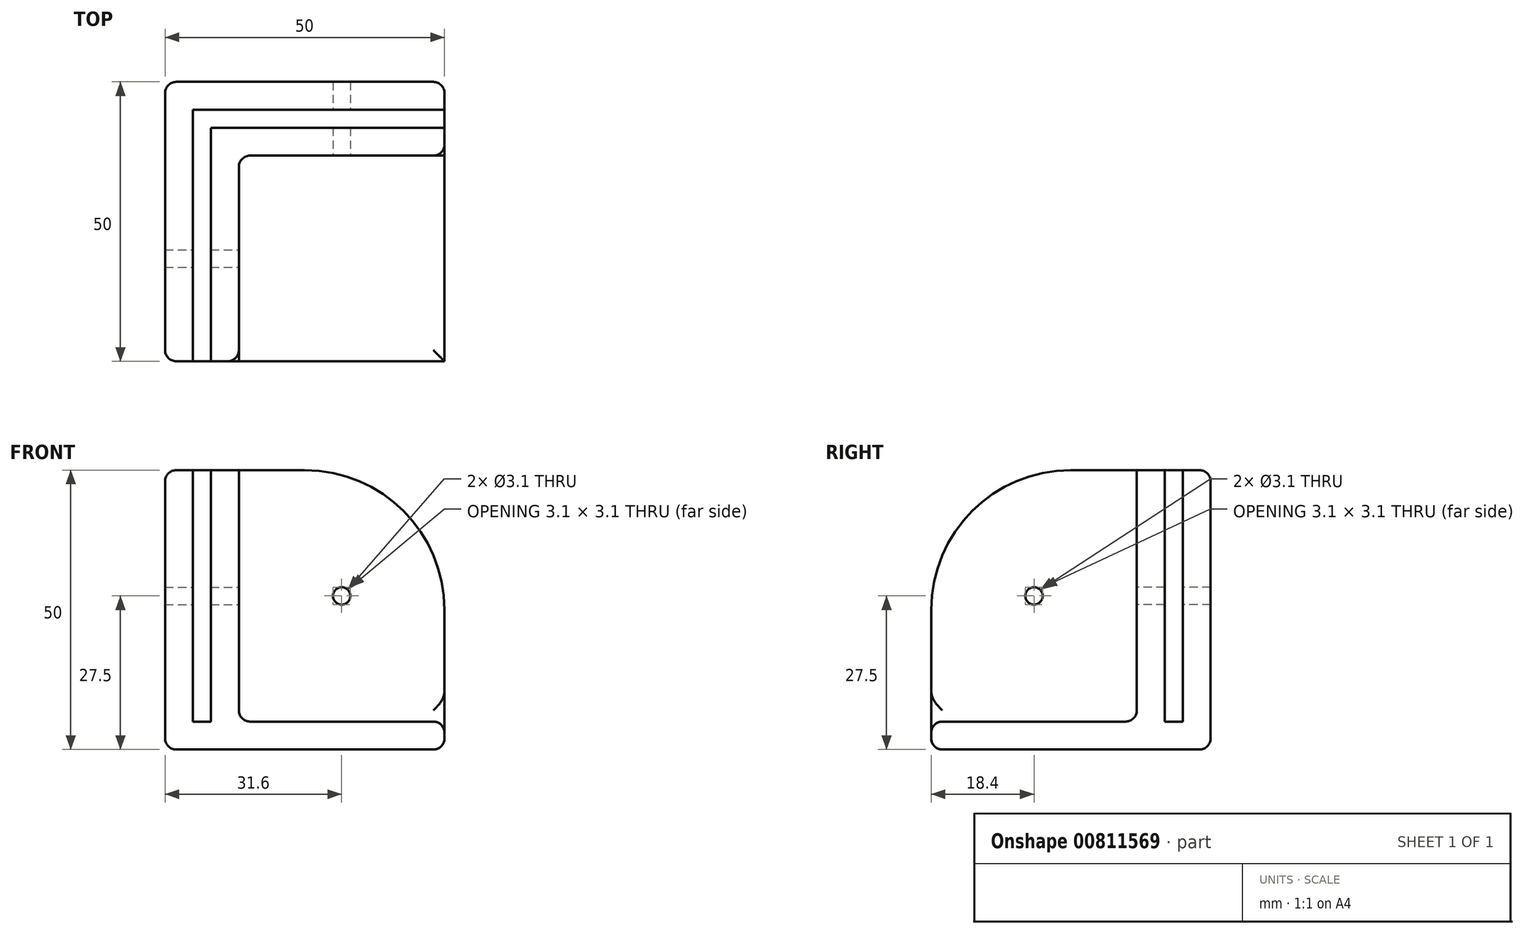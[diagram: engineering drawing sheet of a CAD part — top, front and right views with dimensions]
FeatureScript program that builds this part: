
annotation { "Feature Type Name" : "Feature", "Feature Type Description" : "" }
export const myFeature = defineFeature(function(context is Context, id is Id, definition is map)
    precondition{}
    {
        {
            var Q0;
            Q0=qCreatedBy(makeId("Top.planeOp"),FACE);
            var sketch = newSketch(context, id + "F0", { "sketchPlane" : qUnion([Q0])});
            skLineSegment(sketch, "E0.bottom", {"start": v(25, -25) * mm, "end": v(-25, -25) * mm});
            skLineSegment(sketch, "E0.top", {"start": v(25, 25) * mm, "end": v(-25, 25) * mm});
            skLineSegment(sketch, "E0.left", {"start": v(25, -25) * mm, "end": v(25, 25) * mm});
            skLineSegment(sketch, "E0.right", {"start": v(-25, -25) * mm, "end": v(-25, 25) * mm});
            skPoint(sketch, "E0.middle", {"position": v(0, 0) * mm});
            skSolve(sketch);
        }
        {
            var Q0;
            Q0=qSketchRegion(id+"F0",true);
            extrude(context, id + "F1", {"entities" : qUnion([Q0]), "depth" : 5 * mm, "offsetDistance" : 25 * mm});
        }
        {
            var Q0;
            Q0=makeQuery(id+"F1.opExtrude","CAP_FACE",FACE,{"disambiguationData":[OSD([sQuery(id+"F0.wireOp",EDGE,"E0.bottom"),sQuery(id+"F0.wireOp",EDGE,"E0.top"),sQuery(id+"F0.wireOp",EDGE,"E0.left"),sQuery(id+"F0.wireOp",EDGE,"E0.right")])],"isStart":false});
            var sketch = newSketch(context, id + "F2", { "sketchPlane" : qUnion([Q0])});
            skLineSegment(sketch, "E1.bottom", {"start": v(-25, 25) * mm, "end": v(-20, 25) * mm});
            skLineSegment(sketch, "E1.top", {"start": v(-25, -25) * mm, "end": v(-20, -25) * mm});
            skLineSegment(sketch, "E1.left", {"start": v(-25, 25) * mm, "end": v(-25, -25) * mm});
            skLineSegment(sketch, "E1.right", {"start": v(-20, 25) * mm, "end": v(-20, -25) * mm});
            skLineSegment(sketch, "E2.bottom", {"start": v(-20, 25) * mm, "end": v(25, 25) * mm});
            skLineSegment(sketch, "E2.top", {"start": v(-20, 20) * mm, "end": v(25, 20) * mm});
            skLineSegment(sketch, "E2.left", {"start": v(-20, 25) * mm, "end": v(-20, 20) * mm});
            skLineSegment(sketch, "E2.right", {"start": v(25, 25) * mm, "end": v(25, 20) * mm});
            skSolve(sketch);
        }
        {
            var Q0;
            Q0=qSketchRegion(id+"F2",true);
            extrude(context, id + "F3", {"entities" : qUnion([Q0]), "operationType" : NewBodyOperationType.ADD, "depth" : 45 * mm, "offsetDistance" : 25 * mm});
        }
        {
            var Q0;
            Q0=makeQuery(id+"F1.opExtrude","CAP_FACE",FACE,{"disambiguationData":[OSD([sQuery(id+"F0.wireOp",EDGE,"E0.bottom"),sQuery(id+"F0.wireOp",EDGE,"E0.top"),sQuery(id+"F0.wireOp",EDGE,"E0.left"),sQuery(id+"F0.wireOp",EDGE,"E0.right")])],"isStart":false});
            var sketch = newSketch(context, id + "F4", { "sketchPlane" : qUnion([Q0])});
            skLineSegment(sketch, "E3.bottom", {"start": v(-16.8, -25) * mm, "end": v(-11.8, -25) * mm});
            skLineSegment(sketch, "E3.top", {"start": v(-16.8, 16.8) * mm, "end": v(-11.8, 16.8) * mm});
            skLineSegment(sketch, "E3.left", {"start": v(-16.8, -25) * mm, "end": v(-16.8, 16.8) * mm});
            skLineSegment(sketch, "E3.right", {"start": v(-11.8, -25) * mm, "end": v(-11.8, 16.8) * mm});
            skLineSegment(sketch, "E4.bottom", {"start": v(-11.8, 16.8) * mm, "end": v(25, 16.8) * mm});
            skLineSegment(sketch, "E4.top", {"start": v(-11.8, 11.8) * mm, "end": v(25, 11.8) * mm});
            skLineSegment(sketch, "E4.left", {"start": v(-11.8, 16.8) * mm, "end": v(-11.8, 11.8) * mm});
            skLineSegment(sketch, "E4.right", {"start": v(25, 16.8) * mm, "end": v(25, 11.8) * mm});
            skSolve(sketch);
        }
        {
            var Q0;
            Q0=qSketchRegion(id+"F4",true);
            var Q1;
            Q1=makeQuery(id+"F3.opExtrude","CAP_FACE",FACE,{"disambiguationData":[OSD([sQuery(id+"F2.wireOp",EDGE,"E1.bottom"),sQuery(id+"F2.wireOp",EDGE,"E1.top"),sQuery(id+"F2.wireOp",EDGE,"E1.left"),sQuery(id+"F2.wireOp",EDGE,"E1.right"),sQuery(id+"F2.wireOp",EDGE,"E2.bottom"),sQuery(id+"F2.wireOp",EDGE,"E2.top"),sQuery(id+"F2.wireOp",EDGE,"E2.right")])],"isStart":false});
            extrude(context, id + "F5", {"entities" : qUnion([Q0]), "operationType" : NewBodyOperationType.ADD, "endBound" : BoundingType.UP_TO_SURFACE, "depth" : 25 * mm, "endBoundEntityFace" : qUnion([Q1]), "offsetDistance" : 25 * mm});
        }
        {
            var Q0;
            Q0=makeQuery(id+"F3.opExtrude","CAP_EDGE",EDGE,{"disambiguationData":[OSD([sQuery(id+"F2.wireOp",EDGE,"E1.top")])],"isStart":false});
            var Q1;
            Q1=makeQuery(id+"F5.opExtrude","CAP_EDGE",EDGE,{"disambiguationData":[OSD([sQuery(id+"F4.wireOp",EDGE,"E3.bottom")])],"isStart":false});
            var Q2;
            Q2=makeQuery(id+"F5.opExtrude","CAP_EDGE",EDGE,{"disambiguationData":[OSD([sQuery(id+"F4.wireOp",EDGE,"E4.right")])],"isStart":false});
            var Q3;
            Q3=makeQuery(id+"F3.opExtrude","CAP_EDGE",EDGE,{"disambiguationData":[OSD([sQuery(id+"F2.wireOp",EDGE,"E2.right")])],"isStart":false});
            fillet(context, id + "F6", {"entities" : qUnion([Q0, Q1, Q2, Q3]), "radius" : 25 * mm, "tangentPropagation" : true, "allowEdgeOverflow" : false});
        }
        {
            var Q0;
            Q0=makeQuery(id+"F3.boolean.opBoolean","MERGE",FACE,{"derivedFrom":[makeQuery(id+"F1.opExtrude","SWEPT_FACE",FACE,{"disambiguationData":[OSD([sQuery(id+"F0.wireOp",EDGE,"E0.top")])]}),makeQuery(id+"F3.opExtrude","SWEPT_FACE",FACE,{"disambiguationData":[OSD([sQuery(id+"F2.wireOp",EDGE,"E1.bottom"),sQuery(id+"F2.wireOp",EDGE,"E2.bottom")])]})]});
            var Q1;
            Q1=makeQuery(id+"F1.opExtrude","CAP_FACE",FACE,{"disambiguationData":[OSD([sQuery(id+"F0.wireOp",EDGE,"E0.bottom"),sQuery(id+"F0.wireOp",EDGE,"E0.top"),sQuery(id+"F0.wireOp",EDGE,"E0.left"),sQuery(id+"F0.wireOp",EDGE,"E0.right")])],"isStart":true});
            var Q2;
            Q2=makeQuery(id+"F3.boolean.opBoolean","MERGE",FACE,{"derivedFrom":[makeQuery(id+"F1.opExtrude","SWEPT_FACE",FACE,{"disambiguationData":[OSD([sQuery(id+"F0.wireOp",EDGE,"E0.right")])]}),makeQuery(id+"F3.opExtrude","SWEPT_FACE",FACE,{"disambiguationData":[OSD([sQuery(id+"F2.wireOp",EDGE,"E1.left")])]})]});
            var Q3;
            {var subQ0=sQuery(id+"F0.wireOp",EDGE,"E0.left");var subQ1=sQuery(id+"F0.wireOp",EDGE,"E0.bottom");Q3=makeQuery(id+"F5.boolean.opBoolean","SPLIT",FACE,{"disambiguationData":[TD([makeQuery(id+"F5.opExtrude","SWEPT_FACE",FACE,{"disambiguationData":[OSD([sQuery(id+"F4.wireOp",EDGE,"E3.right")])]})])],"derivedFrom":makeQuery(id+"F1.opExtrude","CAP_FACE",FACE,{"disambiguationData":[OSD([subQ1,sQuery(id+"F0.wireOp",EDGE,"E0.top"),subQ0,sQuery(id+"F0.wireOp",EDGE,"E0.right")])],"isStart":false})});}
            var Q4;
            Q4=makeQuery(id+"F5.opExtrude","SWEPT_EDGE",EDGE,{"disambiguationData":[OSD([sQuery(id+"F4.wireOp",EDGE,"E3.right"),sQuery(id+"F4.wireOp",EDGE,"E4.top"),sQuery(id+"F4.wireOp",EDGE,"E4.left")])]});
            fillet(context, id + "F7", {"entities" : qUnion([Q0, Q1, Q2, Q3, Q4]), "radius" : 2 * mm, "tangentPropagation" : true, "allowEdgeOverflow" : false});
        }
        {
            var Q0;
            Q0=makeQuery(id+"F5.opExtrude","SWEPT_FACE",FACE,{"disambiguationData":[OSD([sQuery(id+"F4.wireOp",EDGE,"E3.right")])]});
            var sketch = newSketch(context, id + "F8", { "sketchPlane" : qUnion([Q0])});
            skPoint(sketch, "E5", {"position": v(-6.6, 27.5) * mm});
            skPoint(sketch, "E5.positionSnap0", {"position": v(-6.6, 7) * mm});
            skPoint(sketch, "E5.positionSnap1", {"position": v(9.8, 27.5) * mm});
            skSolve(sketch);
        }
        {
            var Q0;
            Q0=makeQuery(id+"F5.opExtrude","SWEPT_FACE",FACE,{"disambiguationData":[OSD([sQuery(id+"F4.wireOp",EDGE,"E4.top")])]});
            var sketch = newSketch(context, id + "F9", { "sketchPlane" : qUnion([Q0])});
            skPoint(sketch, "E6", {"position": v(6.6, 27.5) * mm});
            skPoint(sketch, "E6.positionSnap0", {"position": v(-9.8, 27.5) * mm});
            skPoint(sketch, "E6.positionSnap1", {"position": v(6.6, 7) * mm});
            skSolve(sketch);
        }
        {
            var Q0;
            Q0=sQuery(id+"F8.wireOp",VERTEX,"E5");
            var Q1;
            Q1=sQuery(id+"F9.wireOp",VERTEX,"E6");
            var Q2;
            Q2=makeQuery(id+"F1.opExtrude","SWEPT_BODY",BODY,{"disambiguationData":[OSD([sQuery(id+"F0.wireOp",EDGE,"E0.bottom"),sQuery(id+"F0.wireOp",EDGE,"E0.top"),sQuery(id+"F0.wireOp",EDGE,"E0.left"),sQuery(id+"F0.wireOp",EDGE,"E0.right")])]});
            hole(context, id + "F10", {"style" : HoleStyle.SIMPLE, "endStyle" : HoleEndStyle.BLIND, "holeDiameter" : 3.1 * mm, "majorDiameter" : 5 * mm, "holeDepth" : 20 * mm, "isTappedThrough" : true, "tappedDepth" : 12 * mm, "tapClearance" : 3, "locations" : qUnion([Q0, Q1]), "scope" : qUnion([Q2])});
        }
    });
